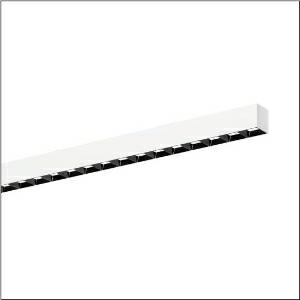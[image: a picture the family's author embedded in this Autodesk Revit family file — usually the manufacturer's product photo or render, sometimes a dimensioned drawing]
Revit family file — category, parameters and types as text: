
# Revit family: silica_r__21_51mx24dc3awb_4576
name_source: partatom
category: Lighting Fixtures
units: mm (PartAtom-declared; Revit-internal decimal feet)

## family parameters
Cut with Voids When Loaded = No
Host = Face
Light Source = No
Part Type = Normal
Room Calculation Point = No
Round Connector Dimension = Use Diameter
Shared = No

## types (1)
- --- (1 x LED, 10800 lm, 79 W, 3000K)
    Apparent Load = 79 VA
    CIE Flux Codes = 74 94 99 100 100
    Color Rendering = 80
    Color Temperature = 3000K
    Default Elevation = 1800 mm
    Description = Silica® 21, office luminaire, primary light control with darklight reflector, of PMMA, black, CAT 2 (L<= 3000cd/m²), light emission: direct distribution, primary light characteristic: asymmetric, installation type: surface-mounted, LED, rated luminous flux: 10.800lm, luminous efficacy: 137lm/W, light colour: 830, colour temperature: 3000K, control gear: DALI 2, with terminal, 3+2-pole, max. 2.5mm², mains connection: 220..240V, AC, 50/60Hz, rated input power: 79W, luminaire housing, of aluminium, traffic white (RAL 9016), length: 3.004mm, width: 53mm, height: 53mm, protection rating (complete): IP20, insulation class (complete): insulation class I (protective earthing), certification: CE, permissible operating ambient temperature: 0..+35°C, standard: EN 50419, packaging unit: 1 piece
    Height = 53 mm
    Lamp = 1 x LED
    Lamp Light Flux = 10800 lm
    Lamp Power = 79 W
    Lamp count = 1
    Length = 3004 mm
    Luminous efficacy = 137 lm/W
    Manufacturer = Siteco
    ModVariant = No
    Model = 51MX24DC3AWB
    Mounting Place = Ceiling
    Mounting Type = Surface mounted
    Number of Poles = 1
    OnlyDefault = Yes
    Power Factor = 1
    Product Name = Silica® 21
    Product group = office luminaire | ceiling mounted
    ProductGroupID = 302
    Protection Class = Protection class I
    Protection Degree = IP 20
    RLX_Detail_Level = 1
    RLX_Emergency_Light_Flux = 0 lm
    RLX_Emergency_Type = 0
    RLX_Emergency_Type_DB = No
    RlxData = <blob elided: 62545 chars, md5=fab6c884>
    Socket = socket
    Standby Power = 0 W
    System Light Flux = 10800 lm
    System Power = 79 W
    Type Comments = factory setting: luminous flux: 100 % | dim-lin: 254 | 448 mA
    Type Image = l_1335873.jpg
    URL = http://relux.com
    VarID = @adj_123076
    Voltage = 0 V
    Weight = 0.00 kg
    Width = 53 mm

## geometry (parser evidence)
native form markers: Blend x4, Sweep x10
no freeform markers — native parametric forms only
